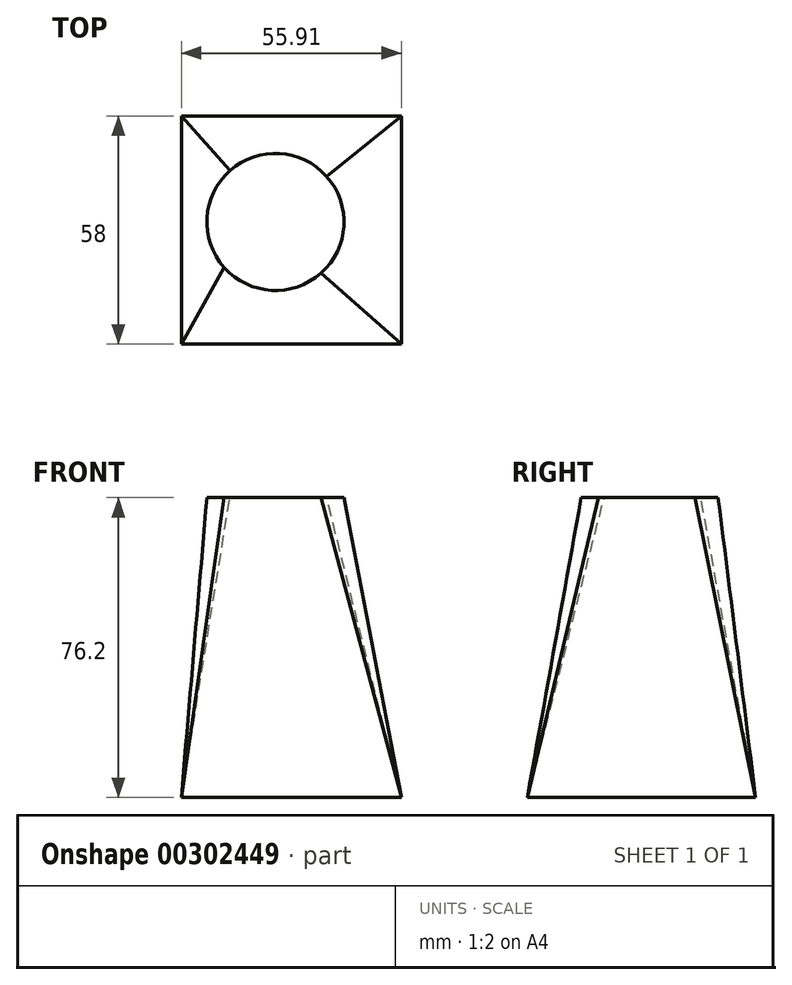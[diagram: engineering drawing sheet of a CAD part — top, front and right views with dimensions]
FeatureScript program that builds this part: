
annotation { "Feature Type Name" : "Feature", "Feature Type Description" : "" }
export const myFeature = defineFeature(function(context is Context, id is Id, definition is map)
    precondition{}
    {
        {
            var Q0;
            Q0=qCreatedBy(makeId("Top.planeOp"),FACE);
            var sketch = newSketch(context, id + "F0", { "sketchPlane" : qUnion([Q0])});
            skLineSegment(sketch, "E0.bottom", {"start": v(-30.04, 31.2) * mm, "end": v(25.87, 31.2) * mm});
            skLineSegment(sketch, "E0.top", {"start": v(-30.04, -26.8) * mm, "end": v(25.87, -26.8) * mm});
            skLineSegment(sketch, "E0.left", {"start": v(-30.04, 31.2) * mm, "end": v(-30.04, -26.8) * mm});
            skLineSegment(sketch, "E0.right", {"start": v(25.87, 31.2) * mm, "end": v(25.87, -26.8) * mm});
            skSolve(sketch);
        }
        {
            var Q0;
            Q0=qCreatedBy(makeId("Top.planeOp"),FACE);
            cPlane(context, id + "F1", {"entities" : qUnion([Q0]), "cplaneType" : CPlaneType.OFFSET, "offset" : 76.2 * mm, "width" : 152.4 * mm, "height" : 152.4 * mm});
        }
        {
            var Q0;
            Q0=qCreatedBy(id+"F1.planeOp",FACE);
            var sketch = newSketch(context, id + "F2", { "sketchPlane" : qUnion([Q0])});
            skCircle(sketch, "E1", {"center": v(-6.13, 4.26) * mm, "radius": 17.41 * mm});
            skSolve(sketch);
        }
        {
            var Q0;
            Q0=makeQuery(id+"F0.imprint","IMPRINT",FACE,{"disambiguationData":[TD([[makeQuery(id+"F0.imprint","IMPRINT",EDGE,{"derivedFrom":sQuery(id+"F0.wireOp",EDGE,"E0.bottom")}),-1.0]])]});
            var Q1;
            Q1=makeQuery(id+"F2.imprint","IMPRINT",FACE,{"disambiguationData":[TD([[makeQuery(id+"F2.imprint","IMPRINT",EDGE,{"derivedFrom":sQuery(id+"F2.wireOp",EDGE,"E1")}),1.0]])]});
            loft(context, id + "F3", {"sheetProfilesArray" : [{ "sheetProfileEntities" : qUnion([Q0]) }, { "sheetProfileEntities" : qUnion([Q1]) }]});
        }
    });
